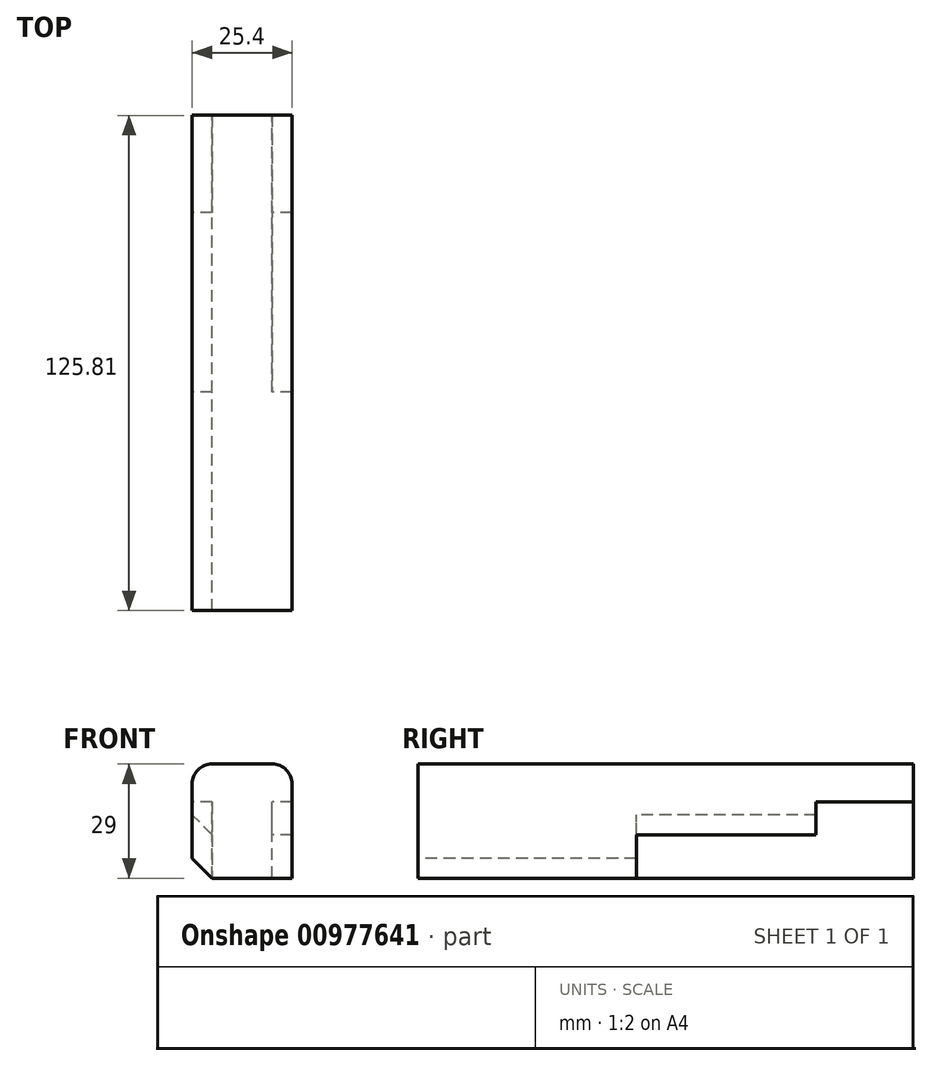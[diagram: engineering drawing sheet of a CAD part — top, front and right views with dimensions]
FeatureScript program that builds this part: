
annotation { "Feature Type Name" : "Feature", "Feature Type Description" : "" }
export const myFeature = defineFeature(function(context is Context, id is Id, definition is map)
    precondition{}
    {
        {
            var Q0;
            Q0=qCreatedBy(makeId("Right.planeOp"),FACE);
            var sketch = newSketch(context, id + "F0", { "sketchPlane" : qUnion([Q0])});
            skLineSegment(sketch, "E0", {"start": v(-55.47, 0) * mm, "end": v(-55.47, -29) * mm});
            skLineSegment(sketch, "E1", {"start": v(-55.47, -29) * mm, "end": v(0, -29) * mm});
            skLineSegment(sketch, "E2", {"start": v(0, -29) * mm, "end": v(0, -18) * mm});
            skLineSegment(sketch, "E3", {"start": v(0, -18) * mm, "end": v(45.66, -18) * mm});
            skLineSegment(sketch, "E4", {"start": v(45.66, -18) * mm, "end": v(45.66, -9.67) * mm});
            skLineSegment(sketch, "E5", {"start": v(45.66, -9.67) * mm, "end": v(70.34, -9.67) * mm});
            skLineSegment(sketch, "E6", {"start": v(70.34, -9.67) * mm, "end": v(70.34, 0) * mm});
            skLineSegment(sketch, "E7", {"start": v(70.34, 0) * mm, "end": v(-55.47, 0) * mm});
            skSolve(sketch);
        }
        {
            var Q0;
            Q0=makeQuery(id+"F0.imprint","IMPRINT",FACE,{"disambiguationData":[TD([[makeQuery(id+"F0.imprint","IMPRINT",EDGE,{"derivedFrom":sQuery(id+"F0.wireOp",EDGE,"E0")}),1.0]])]});
            extrude(context, id + "F1", {"entities" : qUnion([Q0]), "depth" : 25.4 * mm, "offsetDistance" : 25.4 * mm});
        }
        {
            var Q0;
            Q0=makeQuery(id+"F1.opExtrude","CAP_EDGE",EDGE,{"disambiguationData":[OSD([sQuery(id+"F0.wireOp",EDGE,"E7")])],"isStart":false});
            fillet(context, id + "F2", {"entities" : qUnion([Q0]), "radius" : 5.08 * mm, "tangentPropagation" : true, "allowEdgeOverflow" : false});
        }
        {
            var Q0;
            Q0=makeQuery(id+"F1.opExtrude","CAP_EDGE",EDGE,{"disambiguationData":[OSD([sQuery(id+"F0.wireOp",EDGE,"E7")])],"isStart":true});
            fillet(context, id + "F3", {"entities" : qUnion([Q0]), "radius" : 5.08 * mm, "tangentPropagation" : true, "allowEdgeOverflow" : false});
        }
        {
            var Q0;
            Q0=makeQuery(id+"F1.opExtrude","CAP_EDGE",EDGE,{"disambiguationData":[OSD([sQuery(id+"F0.wireOp",EDGE,"E1")])],"isStart":true});
            var Q1;
            Q1=makeQuery(id+"F1.opExtrude","CAP_EDGE",EDGE,{"disambiguationData":[OSD([sQuery(id+"F0.wireOp",EDGE,"E3")])],"isStart":true});
            chamfer(context, id + "F4", {"entities" : qUnion([Q0, Q1]), "width" : 5.08 * mm, "tangentPropagation" : true});
        }
        {
            var Q0;
            Q0=qCreatedBy(makeId("Top.planeOp"),FACE);
            var sketch = newSketch(context, id + "F5", { "sketchPlane" : qUnion([Q0])});
            skCircle(sketch, "E8", {"center": v(12.97, 0) * mm, "radius": 6.33 * mm});
            skSolve(sketch);
        }
        {
            var Q0;
            Q0 = qSketchRegion(id + "F5", true);
            var Q1;
            Q1=makeQuery(id+"F1.opExtrude","SWEPT_FACE",FACE,{"disambiguationData":[OSD([sQuery(id+"F0.wireOp",EDGE,"E7")])]});
            var Q2;
            Q2=makeQuery(id+"F1.opExtrude","SWEPT_FACE",FACE,{"disambiguationData":[OSD([sQuery(id+"F0.wireOp",EDGE,"E1")])]});
            extrude(context, id + "F6", {"entities" : qUnion([Q0, Q1]), "operationType" : NewBodyOperationType.ADD, "endBound" : BoundingType.UP_TO_SURFACE, "oppositeDirection" : true, "depth" : 25.4 * mm, "endBoundEntityFace" : qUnion([Q2]), "offsetDistance" : 25.4 * mm});
        }
    });
